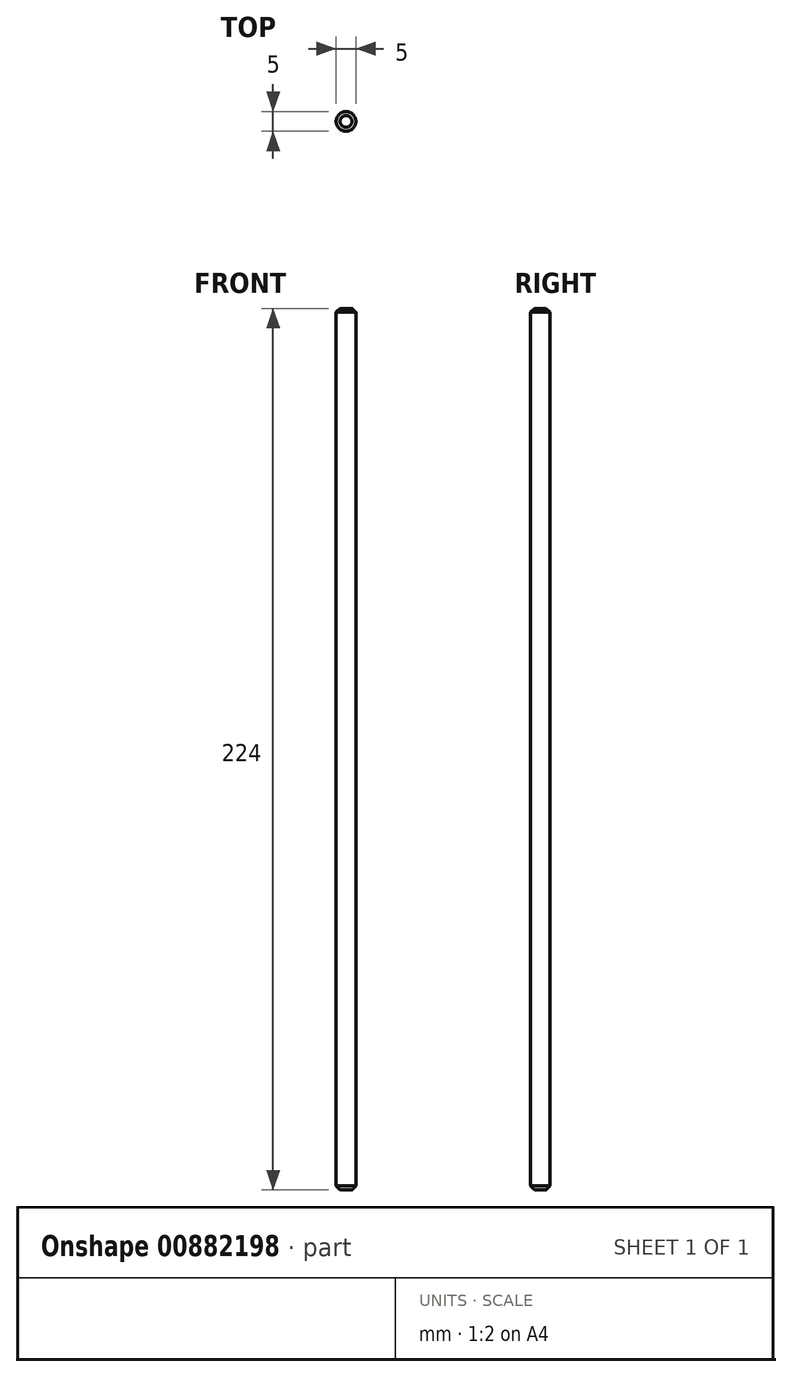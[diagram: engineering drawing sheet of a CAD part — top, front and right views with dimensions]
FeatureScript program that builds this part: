
annotation { "Feature Type Name" : "Feature", "Feature Type Description" : "" }
export const myFeature = defineFeature(function(context is Context, id is Id, definition is map)
    precondition{}
    {
        {
            var Q0;
            Q0=qCreatedBy(makeId("Top.planeOp"),FACE);
            var sketch = newSketch(context, id + "F0", { "sketchPlane" : qUnion([Q0])});
            skCircle(sketch, "E0", {"center": v(0, 0) * mm, "radius": 2.5 * mm});
            skSolve(sketch);
        }
        {
            var Q0;
            Q0 = qSketchRegion(id + "F0", true);
            extrude(context, id + "F1", {"entities" : qUnion([Q0]), "depth" : 224 * mm, "offsetDistance" : 25 * mm});
        }
        {
            var Q0;
            Q0=makeQuery(id+"F1.opExtrude","CAP_EDGE",EDGE,{"disambiguationData":[OSD([sQuery(id+"F0.wireOp",EDGE,"E0")])],"isStart":true});
            var Q1;
            Q1=makeQuery(id+"F1.opExtrude","CAP_EDGE",EDGE,{"disambiguationData":[OSD([sQuery(id+"F0.wireOp",EDGE,"E0")])],"isStart":false});
            chamfer(context, id + "F2", {"entities" : qUnion([Q0, Q1]), "width" : 1 * mm, "tangentPropagation" : true});
        }
    });
